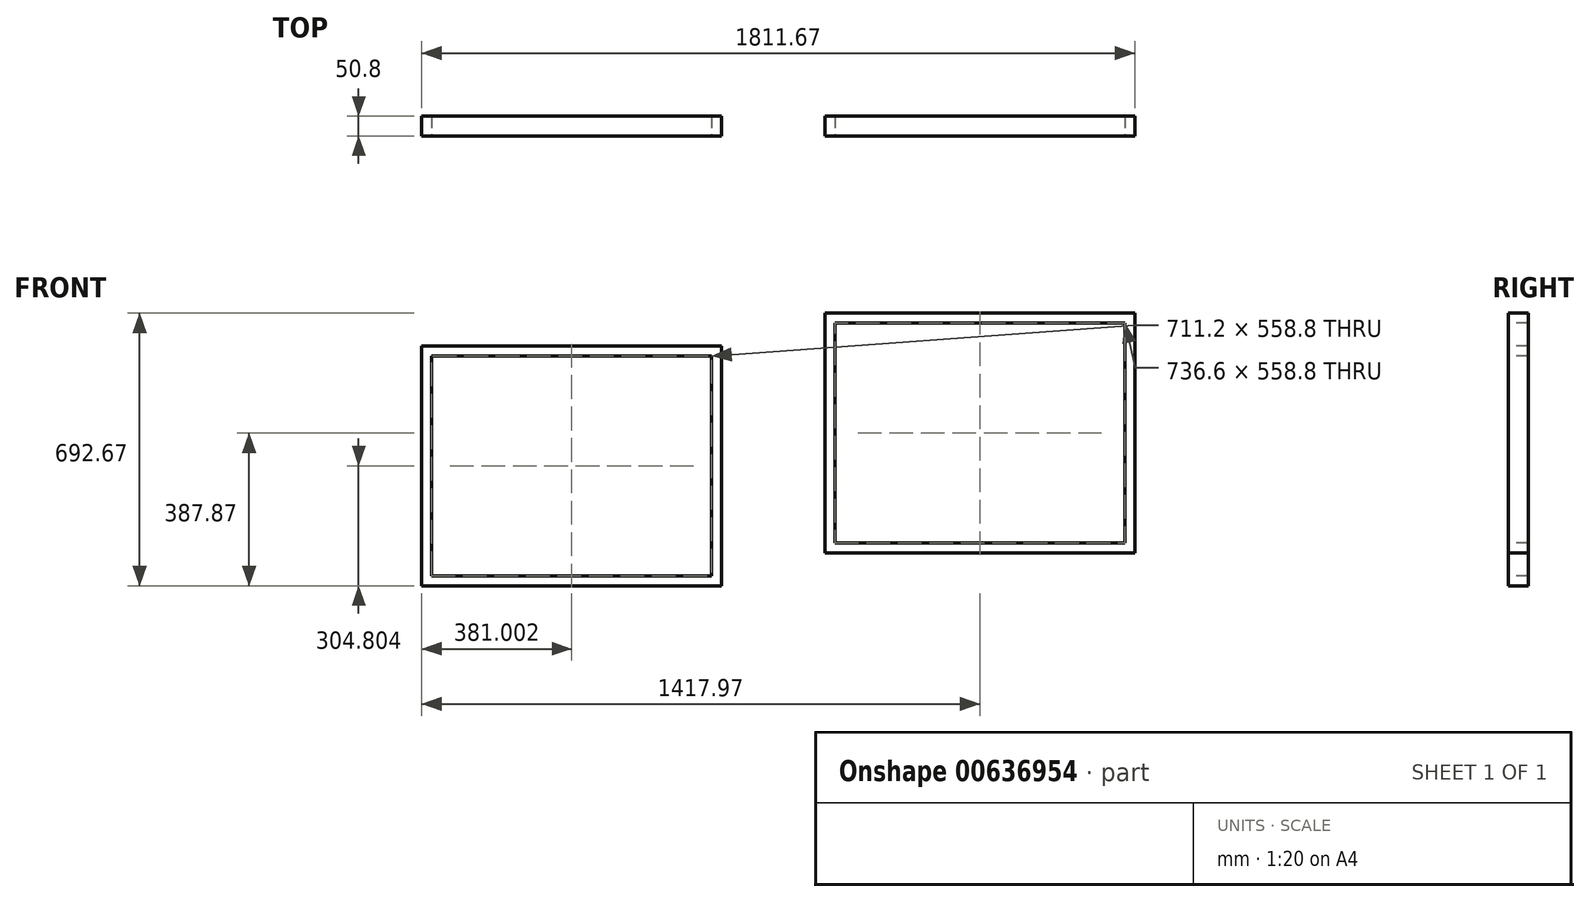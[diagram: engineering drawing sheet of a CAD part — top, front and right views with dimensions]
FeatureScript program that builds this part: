
annotation { "Feature Type Name" : "Feature", "Feature Type Description" : "" }
export const myFeature = defineFeature(function(context is Context, id is Id, definition is map)
    precondition{}
    {
        {
            var Q0;
            Q0=qCreatedBy(makeId("Top.planeOp"),FACE);
            var sketch = newSketch(context, id + "F0", { "sketchPlane" : qUnion([Q0])});
            skLineSegment(sketch, "E0.bottom", {"start": v(-393.7, 138.47) * mm, "end": v(393.7, 138.47) * mm});
            skLineSegment(sketch, "E0.top", {"start": v(-393.7, 189.27) * mm, "end": v(393.7, 189.27) * mm});
            skLineSegment(sketch, "E0.left", {"start": v(-393.7, 138.47) * mm, "end": v(-393.7, 189.27) * mm});
            skLineSegment(sketch, "E0.right", {"start": v(393.7, 138.47) * mm, "end": v(393.7, 189.27) * mm});
            skPoint(sketch, "E0.middle", {"position": v(0, 163.87) * mm});
            skSolve(sketch);
        }
        {
            var Q0;
            Q0 = qSketchRegion(id + "F0", true);
            extrude(context, id + "F1", {"entities" : qUnion([Q0]), "depth" : 609.6 * mm, "offsetDistance" : 25.4 * mm});
        }
        {
            var Q0;
            Q0=makeQuery(id+"F1.opExtrude","SWEPT_FACE",FACE,{"disambiguationData":[OSD([sQuery(id+"F0.wireOp",EDGE,"E0.bottom")])]});
            var sketch = newSketch(context, id + "F2", { "sketchPlane" : qUnion([Q0])});
            skLineSegment(sketch, "E1.bottom", {"start": v(368.3, 25.4) * mm, "end": v(-368.3, 25.4) * mm});
            skLineSegment(sketch, "E1.top", {"start": v(368.3, 584.2) * mm, "end": v(-368.3, 584.2) * mm});
            skLineSegment(sketch, "E1.left", {"start": v(368.3, 25.4) * mm, "end": v(368.3, 584.2) * mm});
            skLineSegment(sketch, "E1.right", {"start": v(-368.3, 25.4) * mm, "end": v(-368.3, 584.2) * mm});
            skPoint(sketch, "E1.middle", {"position": v(0, 304.8) * mm});
            skPoint(sketch, "E1.middle.positionSnap0", {"position": v(0, 609.6) * mm});
            skPoint(sketch, "E1.middle.positionSnap1", {"position": v(393.7, 304.8) * mm});
            skPoint(sketch, "E1.centerSnap0", {"position": v(0, 609.6) * mm});
            skPoint(sketch, "E1.centerSnap1", {"position": v(393.7, 304.8) * mm});
            skSolve(sketch);
        }
        {
            var Q0;
            Q0 = qSketchRegion(id + "F2", true);
            extrude(context, id + "F3", {"entities" : qUnion([Q0]), "operationType" : NewBodyOperationType.REMOVE, "oppositeDirection" : true, "depth" : 50.8 * mm, "offsetDistance" : 25.4 * mm});
        }
        {
            var Q0;
            Q0=makeQuery(id+"F1.opExtrude","SWEPT_FACE",FACE,{"disambiguationData":[OSD([sQuery(id+"F0.wireOp",EDGE,"E0.bottom")])]});
            var sketch = newSketch(context, id + "F4", { "sketchPlane" : qUnion([Q0])});
            skLineSegment(sketch, "E2", {"start": v(-1417.97, 526.53) * mm, "end": v(-655.97, 526.53) * mm});
            skLineSegment(sketch, "E3", {"start": v(-655.97, 526.53) * mm, "end": v(-655.97, -83.07) * mm});
            skLineSegment(sketch, "E4", {"start": v(-655.97, -83.07) * mm, "end": v(-1417.97, -83.07) * mm});
            skLineSegment(sketch, "E5", {"start": v(-1417.97, -83.07) * mm, "end": v(-1417.97, 526.53) * mm});
            skSolve(sketch);
        }
        {
            var Q0;
            Q0=makeQuery(id+"F4.imprint","IMPRINT",FACE,{"disambiguationData":[TD([[makeQuery(id+"F4.imprint","IMPRINT",EDGE,{"derivedFrom":sQuery(id+"F4.wireOp",EDGE,"E2")}),-1.0]])]});
            extrude(context, id + "F5", {"entities" : qUnion([Q0]), "oppositeDirection" : true, "depth" : 50.8 * mm, "offsetDistance" : 25.4 * mm});
        }
        {
            var Q0;
            Q0=makeQuery(id+"F5.opExtrude","CAP_FACE",FACE,{"disambiguationData":[OSD([sQuery(id+"F4.wireOp",EDGE,"E2"),sQuery(id+"F4.wireOp",EDGE,"E3"),sQuery(id+"F4.wireOp",EDGE,"E4"),sQuery(id+"F4.wireOp",EDGE,"E5")])],"isStart":true});
            var sketch = newSketch(context, id + "F6", { "sketchPlane" : qUnion([Q0])});
            skLineSegment(sketch, "E6.bottom", {"start": v(-681.37, -57.67) * mm, "end": v(-1392.57, -57.67) * mm});
            skLineSegment(sketch, "E6.top", {"start": v(-681.37, 501.13) * mm, "end": v(-1392.57, 501.13) * mm});
            skLineSegment(sketch, "E6.left", {"start": v(-681.37, -57.67) * mm, "end": v(-681.37, 501.13) * mm});
            skLineSegment(sketch, "E6.right", {"start": v(-1392.57, -57.67) * mm, "end": v(-1392.57, 501.13) * mm});
            skPoint(sketch, "E6.middle", {"position": v(-1036.97, 221.73) * mm});
            skPoint(sketch, "E6.middle.positionSnap0", {"position": v(-655.97, 221.73) * mm});
            skPoint(sketch, "E6.middle.positionSnap1", {"position": v(-1036.97, 526.53) * mm});
            skPoint(sketch, "E6.centerSnap0", {"position": v(-655.97, 221.73) * mm});
            skPoint(sketch, "E6.centerSnap1", {"position": v(-1036.97, 526.53) * mm});
            skSolve(sketch);
        }
        {
            var Q0;
            Q0=makeQuery(id+"F6.imprint","IMPRINT",FACE,{"disambiguationData":[TD([[makeQuery(id+"F6.imprint","IMPRINT",EDGE,{"derivedFrom":sQuery(id+"F6.wireOp",EDGE,"E6.bottom")}),-1.0]])]});
            extrude(context, id + "F7", {"entities" : qUnion([Q0]), "operationType" : NewBodyOperationType.REMOVE, "oppositeDirection" : true, "depth" : 50.8 * mm, "offsetDistance" : 25.4 * mm});
        }
    });
